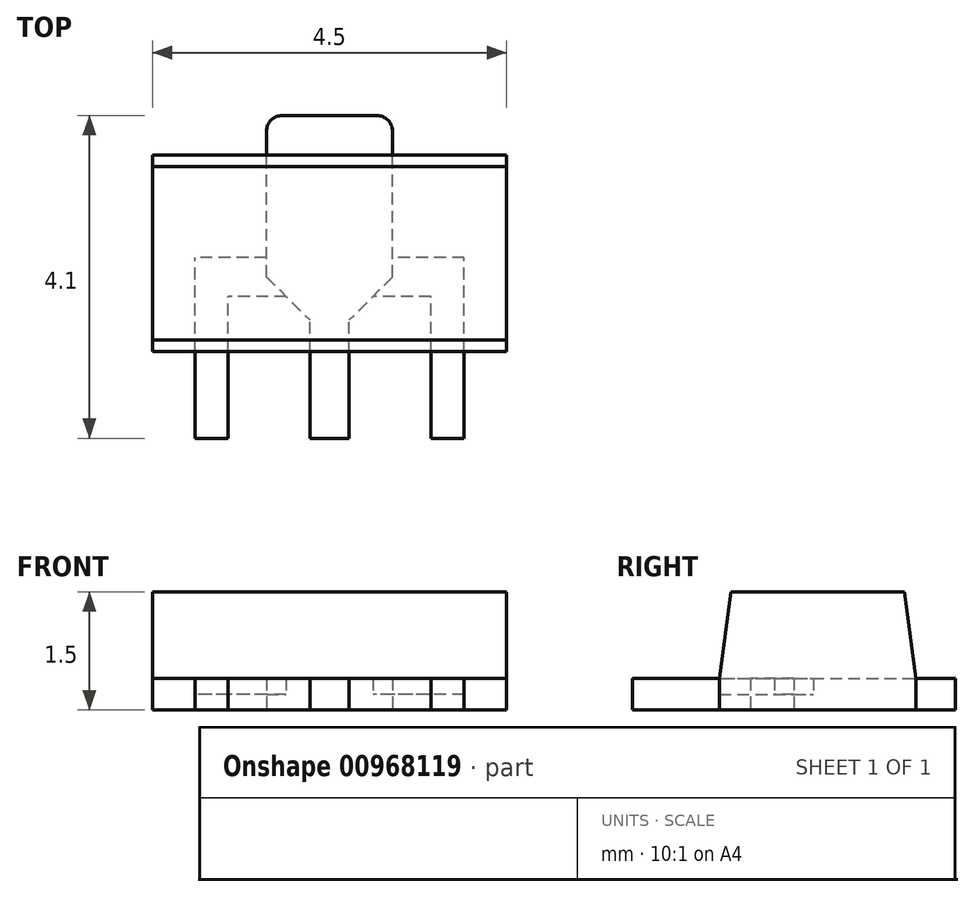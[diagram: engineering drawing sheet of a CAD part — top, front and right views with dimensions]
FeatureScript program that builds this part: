
annotation { "Feature Type Name" : "Feature", "Feature Type Description" : "" }
export const myFeature = defineFeature(function(context is Context, id is Id, definition is map)
    precondition{}
    {
        {
            assignVariable(context, id + "F0", {"name" : "A", "anyValue" : 1.5});
        }
        {
            assignVariable(context, id + "F1", {"name" : "E", "anyValue" : 2.5});
        }
        {
            assignVariable(context, id + "F2", {"name" : "E1", "anyValue" : 2.2});
        }
        {
            assignVariable(context, id + "F3", {"name" : "c", "anyValue" : 0.4});
        }
        {
            var Q0;
            Q0=qCreatedBy(makeId("Top.planeOp"),FACE);
            var sketch = newSketch(context, id + "F4", { "sketchPlane" : qUnion([Q0])});
            skLineSegment(sketch, "E0.bottom", {"start": v(2.25, -1.25) * mm, "end": v(-2.25, -1.25) * mm});
            skLineSegment(sketch, "E0.top", {"start": v(2.25, 1.25) * mm, "end": v(-2.25, 1.25) * mm});
            skLineSegment(sketch, "E0.left", {"start": v(2.25, -1.25) * mm, "end": v(2.25, 1.25) * mm});
            skLineSegment(sketch, "E0.right", {"start": v(-2.25, -1.25) * mm, "end": v(-2.25, 1.25) * mm});
            skPoint(sketch, "E0.middle", {"position": v(0, 0) * mm});
            skLineSegment(sketch, "E1.bottom", {"start": v(0.25, -2.35) * mm, "end": v(-0.25, -2.35) * mm});
            skLineSegment(sketch, "E1.top", {"start": v(0.25, -0.3) * mm, "end": v(-0.25, -0.3) * mm});
            skLineSegment(sketch, "E1.left", {"start": v(0.25, -2.35) * mm, "end": v(0.25, -0.3) * mm});
            skLineSegment(sketch, "E1.right", {"start": v(-0.25, -2.35) * mm, "end": v(-0.25, -0.3) * mm});
            skPoint(sketch, "E1.middle", {"position": v(0, -1.33) * mm});
            skLineSegment(sketch, "E2.bottom", {"start": v(-1.29, -2.35) * mm, "end": v(-1.7, -2.35) * mm});
            skLineSegment(sketch, "E2.top", {"start": v(-1.29, -0.3) * mm, "end": v(-1.71, -0.3) * mm});
            skLineSegment(sketch, "E2.left", {"start": v(-1.29, -2.35) * mm, "end": v(-1.29, -0.3) * mm});
            skLineSegment(sketch, "E2.right", {"start": v(-1.7, -2.35) * mm, "end": v(-1.71, -0.3) * mm});
            skPoint(sketch, "E2.middle", {"position": v(-1.5, -1.33) * mm});
            skLineSegment(sketch, "E3.bottom", {"start": v(1.71, -2.35) * mm, "end": v(1.3, -2.35) * mm});
            skLineSegment(sketch, "E3.top", {"start": v(1.71, -0.3) * mm, "end": v(1.29, -0.3) * mm});
            skLineSegment(sketch, "E3.left", {"start": v(1.71, -2.35) * mm, "end": v(1.71, -0.3) * mm});
            skLineSegment(sketch, "E3.right", {"start": v(1.3, -2.35) * mm, "end": v(1.3, -0.3) * mm});
            skPoint(sketch, "E3.middle", {"position": v(1.5, -1.33) * mm});
            skLineSegment(sketch, "E4.bottom", {"start": v(0.8, -0.3) * mm, "end": v(-0.8, -0.3) * mm});
            skLineSegment(sketch, "E4.top", {"start": v(0.8, 1.75) * mm, "end": v(-0.8, 1.75) * mm});
            skLineSegment(sketch, "E4.left", {"start": v(0.8, -0.3) * mm, "end": v(0.8, 1.75) * mm});
            skLineSegment(sketch, "E4.right", {"start": v(-0.8, -0.3) * mm, "end": v(-0.8, 1.75) * mm});
            skPoint(sketch, "E4.middle", {"position": v(0, 0.72) * mm});
            skLineSegment(sketch, "E5", {"start": v(0, 0.72) * mm, "end": v(0, 0) * mm, "construction": true});
            skLineSegment(sketch, "E6", {"start": v(0, 0) * mm, "end": v(0, -1.33) * mm, "construction": true});
            skLineSegment(sketch, "E7", {"start": v(-1.5, -1.33) * mm, "end": v(0, -1.33) * mm, "construction": true});
            skLineSegment(sketch, "E8", {"start": v(0, -1.33) * mm, "end": v(1.5, -1.33) * mm, "construction": true});
            skLineSegment(sketch, "E9.bottom", {"start": v(1.71, -0.55) * mm, "end": v(-1.7, -0.55) * mm});
            skLineSegment(sketch, "E9.top", {"start": v(1.71, -0.05) * mm, "end": v(-1.7, -0.05) * mm});
            skLineSegment(sketch, "E9.left", {"start": v(1.71, -0.55) * mm, "end": v(1.71, -0.05) * mm});
            skLineSegment(sketch, "E9.right", {"start": v(-1.7, -0.55) * mm, "end": v(-1.7, -0.05) * mm});
            skPoint(sketch, "E9.middle", {"position": v(0, -0.3) * mm});
            skLineSegment(sketch, "E10", {"start": v(-0.8, -0.3) * mm, "end": v(-0.25, -0.85) * mm});
            skLineSegment(sketch, "E11", {"start": v(0.8, -0.3) * mm, "end": v(0.25, -0.85) * mm});
            skSolve(sketch);
        }
        {
            var Q0;
            {var subQ5=sQuery(id+"F4.wireOp",EDGE,"E3.bottom");Q0=makeQuery(id+"F4.imprint","IMPRINT",FACE,{"disambiguationData":[TD([[makeQuery(id+"F4.imprint","IMPRINT",EDGE,{"derivedFrom":subQ5}),-1.0]])]});}
            var Q1;
            {var subQ5=sQuery(id+"F4.wireOp",EDGE,"E1.bottom");Q1=makeQuery(id+"F4.imprint","IMPRINT",FACE,{"disambiguationData":[TD([[makeQuery(id+"F4.imprint","IMPRINT",EDGE,{"derivedFrom":subQ5}),-1.0]])]});}
            var Q2;
            {var subQ0=sQuery(id+"F4.wireOp",EDGE,"E3.right");var subQ1=sQuery(id+"F4.wireOp",EDGE,"E0.bottom");var subQ2=makeQuery(id+"F4.imprint","INTERSECT",VERTEX,{"derivedFrom":[subQ1,subQ0]});Q2=makeQuery(id+"F4.imprint","IMPRINT",FACE,{"disambiguationData":[TD([[makeQuery(id+"F4.imprint","IMPRINT",EDGE,{"disambiguationData":[TD([[subQ2,1.0]])],"derivedFrom":subQ1}),-1.0]])]});}
            var Q3;
            {var subQ9=sQuery(id+"F4.wireOp",EDGE,"E3.top");Q3=makeQuery(id+"F4.imprint","IMPRINT",FACE,{"disambiguationData":[TD([[makeQuery(id+"F4.imprint","IMPRINT",EDGE,{"derivedFrom":subQ9}),-1.0]])]});}
            var Q4;
            {var subQ0=sQuery(id+"F4.wireOp",EDGE,"E3.top");Q4=makeQuery(id+"F4.imprint","IMPRINT",FACE,{"disambiguationData":[TD([[makeQuery(id+"F4.imprint","IMPRINT",EDGE,{"derivedFrom":subQ0}),1.0]])]});}
            var Q5;
            {var subQ0=sQuery(id+"F4.wireOp",EDGE,"E4.left");var subQ1=sQuery(id+"F4.wireOp",EDGE,"E0.top");var subQ2=makeQuery(id+"F4.imprint","INTERSECT",VERTEX,{"derivedFrom":[subQ1,subQ0]});Q5=makeQuery(id+"F4.imprint","IMPRINT",FACE,{"disambiguationData":[TD([[makeQuery(id+"F4.imprint","IMPRINT",EDGE,{"disambiguationData":[TD([[subQ2,-1.0]])],"derivedFrom":subQ1}),1.0]])]});}
            var Q6;
            {var subQ1=sQuery(id+"F4.wireOp",EDGE,"E1.left");var subQ6=sQuery(id+"F4.wireOp",EDGE,"E0.bottom");var subQ7=makeQuery(id+"F4.imprint","INTERSECT",VERTEX,{"derivedFrom":[subQ6,subQ1]});Q6=makeQuery(id+"F4.imprint","IMPRINT",FACE,{"disambiguationData":[TD([[makeQuery(id+"F4.imprint","IMPRINT",EDGE,{"disambiguationData":[TD([[subQ7,-1.0]])],"derivedFrom":subQ6}),-1.0]])]});}
            var Q7;
            {var subQ0=sQuery(id+"F4.wireOp",EDGE,"E1.top");Q7=makeQuery(id+"F4.imprint","IMPRINT",FACE,{"disambiguationData":[TD([[makeQuery(id+"F4.imprint","IMPRINT",EDGE,{"derivedFrom":subQ0}),1.0]])]});}
            var Q8;
            {var subQ1=sQuery(id+"F4.wireOp",EDGE,"E1.top");Q8=makeQuery(id+"F4.imprint","IMPRINT",FACE,{"disambiguationData":[TD([[makeQuery(id+"F4.imprint","IMPRINT",EDGE,{"derivedFrom":subQ1}),-1.0]])]});}
            var Q9;
            {var subQ0=sQuery(id+"F4.wireOp",EDGE,"E2.left");var subQ1=sQuery(id+"F4.wireOp",EDGE,"E0.bottom");var subQ2=makeQuery(id+"F4.imprint","INTERSECT",VERTEX,{"derivedFrom":[subQ1,subQ0]});Q9=makeQuery(id+"F4.imprint","IMPRINT",FACE,{"disambiguationData":[TD([[makeQuery(id+"F4.imprint","IMPRINT",EDGE,{"disambiguationData":[TD([[subQ2,-1.0]])],"derivedFrom":subQ1}),-1.0]])]});}
            var Q10;
            {var subQ0=sQuery(id+"F4.wireOp",EDGE,"E2.top");Q10=makeQuery(id+"F4.imprint","IMPRINT",FACE,{"disambiguationData":[TD([[makeQuery(id+"F4.imprint","IMPRINT",EDGE,{"derivedFrom":subQ0}),1.0]])]});}
            var Q11;
            {var subQ6=sQuery(id+"F4.wireOp",EDGE,"E2.top");Q11=makeQuery(id+"F4.imprint","IMPRINT",FACE,{"disambiguationData":[TD([[makeQuery(id+"F4.imprint","IMPRINT",EDGE,{"derivedFrom":subQ6}),-1.0]])]});}
            var Q12;
            {var subQ5=sQuery(id+"F4.wireOp",EDGE,"E2.bottom");Q12=makeQuery(id+"F4.imprint","IMPRINT",FACE,{"disambiguationData":[TD([[makeQuery(id+"F4.imprint","IMPRINT",EDGE,{"derivedFrom":subQ5}),-1.0]])]});}
            var Q13;
            {var subQ3=sQuery(id+"F4.wireOp",EDGE,"E9.bottom");var subQ5=sQuery(id+"F4.wireOp",EDGE,"E10");var subQ7=makeQuery(id+"F4.imprint","INTERSECT",VERTEX,{"derivedFrom":[subQ3,subQ5]});Q13=makeQuery(id+"F4.imprint","IMPRINT",FACE,{"disambiguationData":[TD([[makeQuery(id+"F4.imprint","IMPRINT",EDGE,{"disambiguationData":[TD([[subQ7,1.0]])],"derivedFrom":subQ3}),-1.0]])]});}
            var Q14;
            {var subQ0=sQuery(id+"F4.wireOp",EDGE,"E10");var subQ1=sQuery(id+"F4.wireOp",EDGE,"E1.right");var subQ2=makeQuery(id+"F4.imprint","INTERSECT",VERTEX,{"derivedFrom":[subQ1,subQ0]});Q14=makeQuery(id+"F4.imprint","IMPRINT",FACE,{"disambiguationData":[TD([[makeQuery(id+"F4.imprint","IMPRINT",EDGE,{"disambiguationData":[TD([[subQ2,-1.0]])],"derivedFrom":subQ1}),1.0]])]});}
            var Q15;
            {var subQ0=sQuery(id+"F4.wireOp",EDGE,"E9.bottom");var subQ1=sQuery(id+"F4.wireOp",EDGE,"E1.left");var subQ2=makeQuery(id+"F4.imprint","INTERSECT",VERTEX,{"derivedFrom":[subQ1,subQ0]});Q15=makeQuery(id+"F4.imprint","IMPRINT",FACE,{"disambiguationData":[TD([[makeQuery(id+"F4.imprint","IMPRINT",EDGE,{"disambiguationData":[TD([[subQ2,1.0]])],"derivedFrom":subQ1}),-1.0]])]});}
            var Q16;
            {var subQ1=sQuery(id+"F4.wireOp",EDGE,"E1.left");var subQ3=sQuery(id+"F4.wireOp",EDGE,"E9.bottom");var subQ4=makeQuery(id+"F4.imprint","INTERSECT",VERTEX,{"derivedFrom":[subQ1,subQ3]});Q16=makeQuery(id+"F4.imprint","IMPRINT",FACE,{"disambiguationData":[TD([[makeQuery(id+"F4.imprint","IMPRINT",EDGE,{"disambiguationData":[TD([[subQ4,1.0]])],"derivedFrom":subQ3}),-1.0]])]});}
            var Q17;
            {var subQ5=sQuery(id+"F4.wireOp",EDGE,"E4.top");Q17=makeQuery(id+"F4.imprint","IMPRINT",FACE,{"disambiguationData":[TD([[makeQuery(id+"F4.imprint","IMPRINT",EDGE,{"derivedFrom":subQ5}),1.0]])]});}
            extrude(context, id + "F5", {"entities" : qUnion([Q0, Q1, Q2, Q3, Q4, Q5, Q6, Q7, Q8, Q9, Q10, Q11, Q12, Q13, Q14, Q15, Q16, Q17]), "depth" : getVariable(context, 'c') * mm, "offsetDistance" : 25 * mm});
        }
        {
            var Q0;
            {var subQ0=sQuery(id+"F4.wireOp",EDGE,"E3.right");var subQ1=sQuery(id+"F4.wireOp",EDGE,"E0.bottom");var subQ2=makeQuery(id+"F4.imprint","INTERSECT",VERTEX,{"derivedFrom":[subQ1,subQ0]});Q0=makeQuery(id+"F4.imprint","IMPRINT",FACE,{"disambiguationData":[TD([[makeQuery(id+"F4.imprint","IMPRINT",EDGE,{"disambiguationData":[TD([[subQ2,1.0]])],"derivedFrom":subQ1}),-1.0]])]});}
            var Q1;
            {var subQ0=sQuery(id+"F4.wireOp",EDGE,"E3.top");Q1=makeQuery(id+"F4.imprint","IMPRINT",FACE,{"disambiguationData":[TD([[makeQuery(id+"F4.imprint","IMPRINT",EDGE,{"derivedFrom":subQ0}),1.0]])]});}
            var Q2;
            {var subQ9=sQuery(id+"F4.wireOp",EDGE,"E3.top");Q2=makeQuery(id+"F4.imprint","IMPRINT",FACE,{"disambiguationData":[TD([[makeQuery(id+"F4.imprint","IMPRINT",EDGE,{"derivedFrom":subQ9}),-1.0]])]});}
            var Q3;
            {var subQ0=sQuery(id+"F4.wireOp",EDGE,"E2.left");var subQ1=sQuery(id+"F4.wireOp",EDGE,"E0.bottom");var subQ2=makeQuery(id+"F4.imprint","INTERSECT",VERTEX,{"derivedFrom":[subQ1,subQ0]});Q3=makeQuery(id+"F4.imprint","IMPRINT",FACE,{"disambiguationData":[TD([[makeQuery(id+"F4.imprint","IMPRINT",EDGE,{"disambiguationData":[TD([[subQ2,-1.0]])],"derivedFrom":subQ1}),-1.0]])]});}
            var Q4;
            {var subQ0=sQuery(id+"F4.wireOp",EDGE,"E2.top");Q4=makeQuery(id+"F4.imprint","IMPRINT",FACE,{"disambiguationData":[TD([[makeQuery(id+"F4.imprint","IMPRINT",EDGE,{"derivedFrom":subQ0}),1.0]])]});}
            var Q5;
            {var subQ6=sQuery(id+"F4.wireOp",EDGE,"E2.top");Q5=makeQuery(id+"F4.imprint","IMPRINT",FACE,{"disambiguationData":[TD([[makeQuery(id+"F4.imprint","IMPRINT",EDGE,{"derivedFrom":subQ6}),-1.0]])]});}
            extrude(context, id + "F6", {"entities" : qUnion([Q0, Q1, Q2, Q3, Q4, Q5]), "operationType" : NewBodyOperationType.REMOVE, "depth" : (getVariable(context, 'c') / 2) * mm, "offsetDistance" : 25 * mm});
        }
        {
            var Q0;
            Q0=makeQuery(id+"F5.opExtrude","SWEPT_EDGE",EDGE,{"disambiguationData":[OSD([sQuery(id+"F4.wireOp",EDGE,"E4.top"),sQuery(id+"F4.wireOp",EDGE,"E4.left")])]});
            var Q1;
            Q1=makeQuery(id+"F5.opExtrude","SWEPT_EDGE",EDGE,{"disambiguationData":[OSD([sQuery(id+"F4.wireOp",EDGE,"E4.top"),sQuery(id+"F4.wireOp",EDGE,"E4.right")])]});
            fillet(context, id + "F7", {"entities" : qUnion([Q0, Q1]), "radius" : getVariable(context, 'c') / 2 * mm, "tangentPropagation" : true, "allowEdgeOverflow" : false});
        }
        {
            var Q0;
            {var subQ0=sQuery(id+"F4.wireOp",EDGE,"E0.right");Q0=makeQuery(id+"F4.imprint","IMPRINT",FACE,{"disambiguationData":[TD([[makeQuery(id+"F4.imprint","IMPRINT",EDGE,{"derivedFrom":subQ0}),-1.0]])]});}
            var Q1;
            {var subQ0=sQuery(id+"F4.wireOp",EDGE,"E0.left");Q1=makeQuery(id+"F4.imprint","IMPRINT",FACE,{"disambiguationData":[TD([[makeQuery(id+"F4.imprint","IMPRINT",EDGE,{"derivedFrom":subQ0}),1.0]])]});}
            var Q2;
            {var subQ0=sQuery(id+"F4.wireOp",EDGE,"E4.left");var subQ1=sQuery(id+"F4.wireOp",EDGE,"E0.top");var subQ2=makeQuery(id+"F4.imprint","INTERSECT",VERTEX,{"derivedFrom":[subQ1,subQ0]});Q2=makeQuery(id+"F4.imprint","IMPRINT",FACE,{"disambiguationData":[TD([[makeQuery(id+"F4.imprint","IMPRINT",EDGE,{"disambiguationData":[TD([[subQ2,-1.0]])],"derivedFrom":subQ1}),1.0]])]});}
            var Q3;
            {var subQ5=sQuery(id+"F4.wireOp",EDGE,"E1.right");var subQ7=sQuery(id+"F4.wireOp",EDGE,"E0.bottom");var subQ9=makeQuery(id+"F4.imprint","INTERSECT",VERTEX,{"derivedFrom":[subQ7,subQ5]});Q3=makeQuery(id+"F4.imprint","IMPRINT",FACE,{"disambiguationData":[TD([[makeQuery(id+"F4.imprint","IMPRINT",EDGE,{"disambiguationData":[TD([[subQ9,-1.0]])],"derivedFrom":subQ7}),-1.0]])]});}
            var Q4;
            {var subQ1=sQuery(id+"F4.wireOp",EDGE,"E3.right");var subQ5=sQuery(id+"F4.wireOp",EDGE,"E0.bottom");var subQ6=makeQuery(id+"F4.imprint","INTERSECT",VERTEX,{"derivedFrom":[subQ5,subQ1]});Q4=makeQuery(id+"F4.imprint","IMPRINT",FACE,{"disambiguationData":[TD([[makeQuery(id+"F4.imprint","IMPRINT",EDGE,{"disambiguationData":[TD([[subQ6,-1.0]])],"derivedFrom":subQ5}),-1.0]])]});}
            var Q5;
            {var subQ0=sQuery(id+"F4.wireOp",EDGE,"E2.left");var subQ1=sQuery(id+"F4.wireOp",EDGE,"E0.bottom");var subQ2=makeQuery(id+"F4.imprint","INTERSECT",VERTEX,{"derivedFrom":[subQ1,subQ0]});Q5=makeQuery(id+"F4.imprint","IMPRINT",FACE,{"disambiguationData":[TD([[makeQuery(id+"F4.imprint","IMPRINT",EDGE,{"disambiguationData":[TD([[subQ2,-1.0]])],"derivedFrom":subQ1}),-1.0]])]});}
            var Q6;
            {var subQ0=sQuery(id+"F4.wireOp",EDGE,"E2.top");Q6=makeQuery(id+"F4.imprint","IMPRINT",FACE,{"disambiguationData":[TD([[makeQuery(id+"F4.imprint","IMPRINT",EDGE,{"derivedFrom":subQ0}),1.0]])]});}
            var Q7;
            {var subQ6=sQuery(id+"F4.wireOp",EDGE,"E2.top");Q7=makeQuery(id+"F4.imprint","IMPRINT",FACE,{"disambiguationData":[TD([[makeQuery(id+"F4.imprint","IMPRINT",EDGE,{"derivedFrom":subQ6}),-1.0]])]});}
            var Q8;
            {var subQ1=sQuery(id+"F4.wireOp",EDGE,"E1.top");Q8=makeQuery(id+"F4.imprint","IMPRINT",FACE,{"disambiguationData":[TD([[makeQuery(id+"F4.imprint","IMPRINT",EDGE,{"derivedFrom":subQ1}),-1.0]])]});}
            var Q9;
            {var subQ3=sQuery(id+"F4.wireOp",EDGE,"E9.bottom");var subQ5=sQuery(id+"F4.wireOp",EDGE,"E10");var subQ7=makeQuery(id+"F4.imprint","INTERSECT",VERTEX,{"derivedFrom":[subQ3,subQ5]});Q9=makeQuery(id+"F4.imprint","IMPRINT",FACE,{"disambiguationData":[TD([[makeQuery(id+"F4.imprint","IMPRINT",EDGE,{"disambiguationData":[TD([[subQ7,1.0]])],"derivedFrom":subQ3}),-1.0]])]});}
            var Q10;
            {var subQ1=sQuery(id+"F4.wireOp",EDGE,"E1.left");var subQ6=sQuery(id+"F4.wireOp",EDGE,"E0.bottom");var subQ7=makeQuery(id+"F4.imprint","INTERSECT",VERTEX,{"derivedFrom":[subQ6,subQ1]});Q10=makeQuery(id+"F4.imprint","IMPRINT",FACE,{"disambiguationData":[TD([[makeQuery(id+"F4.imprint","IMPRINT",EDGE,{"disambiguationData":[TD([[subQ7,-1.0]])],"derivedFrom":subQ6}),-1.0]])]});}
            var Q11;
            {var subQ0=sQuery(id+"F4.wireOp",EDGE,"E10");var subQ1=sQuery(id+"F4.wireOp",EDGE,"E1.right");var subQ2=makeQuery(id+"F4.imprint","INTERSECT",VERTEX,{"derivedFrom":[subQ1,subQ0]});Q11=makeQuery(id+"F4.imprint","IMPRINT",FACE,{"disambiguationData":[TD([[makeQuery(id+"F4.imprint","IMPRINT",EDGE,{"disambiguationData":[TD([[subQ2,-1.0]])],"derivedFrom":subQ1}),1.0]])]});}
            var Q12;
            {var subQ0=sQuery(id+"F4.wireOp",EDGE,"E1.top");Q12=makeQuery(id+"F4.imprint","IMPRINT",FACE,{"disambiguationData":[TD([[makeQuery(id+"F4.imprint","IMPRINT",EDGE,{"derivedFrom":subQ0}),1.0]])]});}
            var Q13;
            {var subQ1=sQuery(id+"F4.wireOp",EDGE,"E1.left");var subQ3=sQuery(id+"F4.wireOp",EDGE,"E9.bottom");var subQ4=makeQuery(id+"F4.imprint","INTERSECT",VERTEX,{"derivedFrom":[subQ1,subQ3]});Q13=makeQuery(id+"F4.imprint","IMPRINT",FACE,{"disambiguationData":[TD([[makeQuery(id+"F4.imprint","IMPRINT",EDGE,{"disambiguationData":[TD([[subQ4,1.0]])],"derivedFrom":subQ3}),-1.0]])]});}
            var Q14;
            {var subQ9=sQuery(id+"F4.wireOp",EDGE,"E3.top");Q14=makeQuery(id+"F4.imprint","IMPRINT",FACE,{"disambiguationData":[TD([[makeQuery(id+"F4.imprint","IMPRINT",EDGE,{"derivedFrom":subQ9}),-1.0]])]});}
            var Q15;
            {var subQ0=sQuery(id+"F4.wireOp",EDGE,"E9.bottom");var subQ1=sQuery(id+"F4.wireOp",EDGE,"E1.left");var subQ2=makeQuery(id+"F4.imprint","INTERSECT",VERTEX,{"derivedFrom":[subQ1,subQ0]});Q15=makeQuery(id+"F4.imprint","IMPRINT",FACE,{"disambiguationData":[TD([[makeQuery(id+"F4.imprint","IMPRINT",EDGE,{"disambiguationData":[TD([[subQ2,1.0]])],"derivedFrom":subQ1}),-1.0]])]});}
            var Q16;
            {var subQ0=sQuery(id+"F4.wireOp",EDGE,"E3.right");var subQ1=sQuery(id+"F4.wireOp",EDGE,"E0.bottom");var subQ2=makeQuery(id+"F4.imprint","INTERSECT",VERTEX,{"derivedFrom":[subQ1,subQ0]});Q16=makeQuery(id+"F4.imprint","IMPRINT",FACE,{"disambiguationData":[TD([[makeQuery(id+"F4.imprint","IMPRINT",EDGE,{"disambiguationData":[TD([[subQ2,1.0]])],"derivedFrom":subQ1}),-1.0]])]});}
            var Q17;
            {var subQ0=sQuery(id+"F4.wireOp",EDGE,"E3.top");Q17=makeQuery(id+"F4.imprint","IMPRINT",FACE,{"disambiguationData":[TD([[makeQuery(id+"F4.imprint","IMPRINT",EDGE,{"derivedFrom":subQ0}),1.0]])]});}
            extrude(context, id + "F8", {"entities" : qUnion([Q0, Q1, Q2, Q3, Q4, Q5, Q6, Q7, Q8, Q9, Q10, Q11, Q12, Q13, Q14, Q15, Q16, Q17]), "depth" : (getVariable(context, 'A')) * mm, "offsetDistance" : 25 * mm});
        }
        {
            var Q0;
            Q0=makeQuery(id+"F8.opExtrude","CAP_EDGE",EDGE,{"disambiguationData":[OSD([sQuery(id+"F4.wireOp",EDGE,"E0.top")])],"isStart":false});
            var Q1;
            Q1=makeQuery(id+"F8.opExtrude","CAP_EDGE",EDGE,{"disambiguationData":[OSD([sQuery(id+"F4.wireOp",EDGE,"E0.bottom")])],"isStart":false});
            chamfer(context, id + "F9", {"entities" : qUnion([Q0, Q1]), "chamferType" : ChamferType.TWO_OFFSETS, "width1" : (getVariable(context, 'A') - getVariable(context, 'c')) * mm, "oppositeDirection" : true, "width2" : (getVariable(context, 'E') - getVariable(context, 'E1')) / 2 * mm, "tangentPropagation" : true});
        }
        {
            var Q0;
            {var subQ0=sQuery(id+"F4.wireOp",EDGE,"E4.left");var subQ1=sQuery(id+"F4.wireOp",EDGE,"E0.top");var subQ2=makeQuery(id+"F4.imprint","INTERSECT",VERTEX,{"derivedFrom":[subQ1,subQ0]});Q0=makeQuery(id+"F4.imprint","IMPRINT",FACE,{"disambiguationData":[TD([[makeQuery(id+"F4.imprint","IMPRINT",EDGE,{"disambiguationData":[TD([[subQ2,-1.0]])],"derivedFrom":subQ1}),1.0]])]});}
            var Q1;
            {var subQ1=sQuery(id+"F4.wireOp",EDGE,"E1.top");Q1=makeQuery(id+"F4.imprint","IMPRINT",FACE,{"disambiguationData":[TD([[makeQuery(id+"F4.imprint","IMPRINT",EDGE,{"derivedFrom":subQ1}),-1.0]])]});}
            var Q2;
            {var subQ3=sQuery(id+"F4.wireOp",EDGE,"E9.bottom");var subQ5=sQuery(id+"F4.wireOp",EDGE,"E10");var subQ7=makeQuery(id+"F4.imprint","INTERSECT",VERTEX,{"derivedFrom":[subQ3,subQ5]});Q2=makeQuery(id+"F4.imprint","IMPRINT",FACE,{"disambiguationData":[TD([[makeQuery(id+"F4.imprint","IMPRINT",EDGE,{"disambiguationData":[TD([[subQ7,1.0]])],"derivedFrom":subQ3}),-1.0]])]});}
            var Q3;
            {var subQ0=sQuery(id+"F4.wireOp",EDGE,"E10");var subQ1=sQuery(id+"F4.wireOp",EDGE,"E1.right");var subQ2=makeQuery(id+"F4.imprint","INTERSECT",VERTEX,{"derivedFrom":[subQ1,subQ0]});Q3=makeQuery(id+"F4.imprint","IMPRINT",FACE,{"disambiguationData":[TD([[makeQuery(id+"F4.imprint","IMPRINT",EDGE,{"disambiguationData":[TD([[subQ2,-1.0]])],"derivedFrom":subQ1}),1.0]])]});}
            var Q4;
            {var subQ1=sQuery(id+"F4.wireOp",EDGE,"E1.left");var subQ6=sQuery(id+"F4.wireOp",EDGE,"E0.bottom");var subQ7=makeQuery(id+"F4.imprint","INTERSECT",VERTEX,{"derivedFrom":[subQ6,subQ1]});Q4=makeQuery(id+"F4.imprint","IMPRINT",FACE,{"disambiguationData":[TD([[makeQuery(id+"F4.imprint","IMPRINT",EDGE,{"disambiguationData":[TD([[subQ7,-1.0]])],"derivedFrom":subQ6}),-1.0]])]});}
            var Q5;
            {var subQ0=sQuery(id+"F4.wireOp",EDGE,"E1.top");Q5=makeQuery(id+"F4.imprint","IMPRINT",FACE,{"disambiguationData":[TD([[makeQuery(id+"F4.imprint","IMPRINT",EDGE,{"derivedFrom":subQ0}),1.0]])]});}
            var Q6;
            {var subQ1=sQuery(id+"F4.wireOp",EDGE,"E1.left");var subQ3=sQuery(id+"F4.wireOp",EDGE,"E9.bottom");var subQ4=makeQuery(id+"F4.imprint","INTERSECT",VERTEX,{"derivedFrom":[subQ1,subQ3]});Q6=makeQuery(id+"F4.imprint","IMPRINT",FACE,{"disambiguationData":[TD([[makeQuery(id+"F4.imprint","IMPRINT",EDGE,{"disambiguationData":[TD([[subQ4,1.0]])],"derivedFrom":subQ3}),-1.0]])]});}
            var Q7;
            {var subQ0=sQuery(id+"F4.wireOp",EDGE,"E9.bottom");var subQ1=sQuery(id+"F4.wireOp",EDGE,"E1.left");var subQ2=makeQuery(id+"F4.imprint","INTERSECT",VERTEX,{"derivedFrom":[subQ1,subQ0]});Q7=makeQuery(id+"F4.imprint","IMPRINT",FACE,{"disambiguationData":[TD([[makeQuery(id+"F4.imprint","IMPRINT",EDGE,{"disambiguationData":[TD([[subQ2,1.0]])],"derivedFrom":subQ1}),-1.0]])]});}
            extrude(context, id + "F10", {"entities" : qUnion([Q0, Q1, Q2, Q3, Q4, Q5, Q6, Q7]), "operationType" : NewBodyOperationType.REMOVE, "depth" : getVariable(context, 'c') * mm, "offsetDistance" : 25 * mm});
        }
        {
            var Q0;
            {var subQ0=sQuery(id+"F4.wireOp",EDGE,"E4.left");var subQ1=sQuery(id+"F4.wireOp",EDGE,"E0.top");var subQ2=makeQuery(id+"F4.imprint","INTERSECT",VERTEX,{"derivedFrom":[subQ1,subQ0]});Q0=makeQuery(id+"F4.imprint","IMPRINT",FACE,{"disambiguationData":[TD([[makeQuery(id+"F4.imprint","IMPRINT",EDGE,{"disambiguationData":[TD([[subQ2,-1.0]])],"derivedFrom":subQ1}),1.0]])]});}
            var sketch = newSketch(context, id + "F11", { "sketchPlane" : qUnion([Q0])});
            skLineSegment(sketch, "E12.bottom", {"start": v(-1.95, -2.6) * mm, "end": v(1.95, -2.6) * mm, "construction": true});
            skLineSegment(sketch, "E12.top", {"start": v(-1.95, 2) * mm, "end": v(1.95, 2) * mm, "construction": true});
            skLineSegment(sketch, "E12.left", {"start": v(-1.95, -2.6) * mm, "end": v(-1.95, 2) * mm, "construction": true});
            skLineSegment(sketch, "E12.right", {"start": v(1.95, -2.6) * mm, "end": v(1.95, 2) * mm, "construction": true});
            skPoint(sketch, "E12.middle", {"position": v(0, -0.3) * mm});
            skLineSegment(sketch, "E13.bottom", {"start": v(0.45, -1.13) * mm, "end": v(-0.45, -1.13) * mm});
            skLineSegment(sketch, "E13.top", {"start": v(0.45, -2.6) * mm, "end": v(-0.45, -2.6) * mm});
            skLineSegment(sketch, "E13.left", {"start": v(0.45, -1.13) * mm, "end": v(0.45, -2.6) * mm});
            skLineSegment(sketch, "E13.right", {"start": v(-0.45, -1.13) * mm, "end": v(-0.45, -2.6) * mm});
            skPoint(sketch, "E13.middle", {"position": v(0, -1.86) * mm});
            skLineSegment(sketch, "E14.bottom", {"start": v(1.05, -2.6) * mm, "end": v(1.95, -2.6) * mm});
            skLineSegment(sketch, "E14.top", {"start": v(1.05, -1.3) * mm, "end": v(1.95, -1.3) * mm});
            skLineSegment(sketch, "E14.left", {"start": v(1.05, -2.6) * mm, "end": v(1.05, -1.3) * mm});
            skLineSegment(sketch, "E14.right", {"start": v(1.95, -2.6) * mm, "end": v(1.95, -1.3) * mm});
            skPoint(sketch, "E14.middle", {"position": v(1.5, -1.95) * mm});
            skLineSegment(sketch, "E15.bottom", {"start": v(-1.95, -2.6) * mm, "end": v(-1.05, -2.6) * mm});
            skLineSegment(sketch, "E15.top", {"start": v(-1.95, -1.3) * mm, "end": v(-1.05, -1.3) * mm});
            skLineSegment(sketch, "E15.left", {"start": v(-1.95, -2.6) * mm, "end": v(-1.95, -1.3) * mm});
            skLineSegment(sketch, "E15.right", {"start": v(-1.05, -2.6) * mm, "end": v(-1.05, -1.3) * mm});
            skPoint(sketch, "E15.middle", {"position": v(-1.5, -1.95) * mm});
            skLineSegment(sketch, "E16.bottom", {"start": v(-0.87, -1.13) * mm, "end": v(0.87, -1.13) * mm});
            skLineSegment(sketch, "E16.top", {"start": v(-0.87, 2) * mm, "end": v(0.87, 2) * mm});
            skLineSegment(sketch, "E16.left", {"start": v(-0.87, -1.13) * mm, "end": v(-0.87, 2) * mm});
            skLineSegment(sketch, "E16.right", {"start": v(0.87, -1.13) * mm, "end": v(0.87, 2) * mm});
            skPoint(sketch, "E16.middle", {"position": v(0, 0.44) * mm});
            skSolve(sketch);
        }
    });
